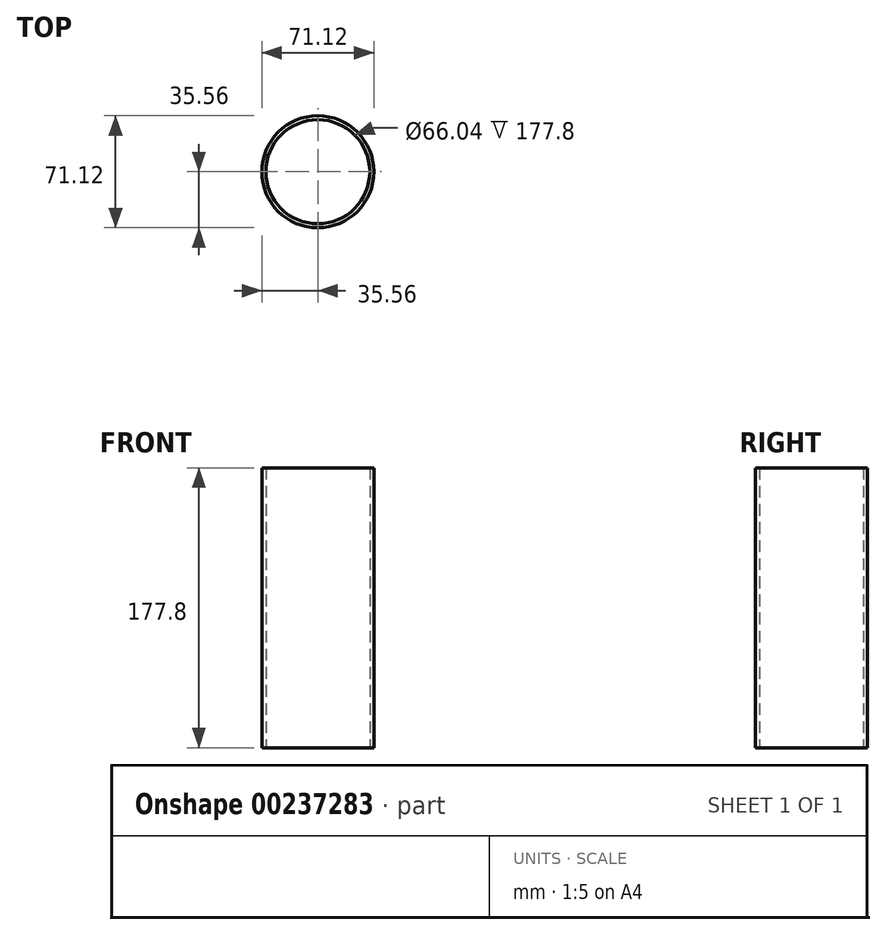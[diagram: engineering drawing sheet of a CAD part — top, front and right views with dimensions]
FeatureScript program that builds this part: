
annotation { "Feature Type Name" : "Feature", "Feature Type Description" : "" }
export const myFeature = defineFeature(function(context is Context, id is Id, definition is map)
    precondition{}
    {
        {
            var Q0;
            Q0=qCreatedBy(makeId("Top.planeOp"),FACE);
            var sketch = newSketch(context, id + "F0", { "sketchPlane" : qUnion([Q0])});
            skCircle(sketch, "E0", {"center": v(0, 0) * mm, "radius": 35.56 * mm});
            skCircle(sketch, "E1", {"center": v(0, 0) * mm, "radius": 33.02 * mm});
            skSolve(sketch);
        }
        {
            var Q0;
            Q0=makeQuery(id+"F0.imprint","IMPRINT",FACE,{"disambiguationData":[TD([[makeQuery(id+"F0.imprint","IMPRINT",EDGE,{"derivedFrom":sQuery(id+"F0.wireOp",EDGE,"E0")}),1.0]])]});
            extrude(context, id + "F1", {"entities" : qUnion([Q0]), "depth" : 177.8 * mm});
        }
    });
